# Revit family: RFL5
name_source: partatom
category: Lighting Fixtures
revit_build: Autodesk Revit 2014 (Build: 20130308_1515(x64)
units: mm (PartAtom-declared; Revit-internal decimal feet)

## types (1)
- RFL4
    Apparent Load = 265 VA
    Assembly Code = D5020200
    Certifications = UL 1598 Standard for Luminaires,IP66 certified.
    Color Filter = 16777215
    Connector Description = Lighting Connector
    Default Elevation = 48 "
    Description = Large LED flood with a variety of NEMA distribution for lighting applications such as safety/security, accent, flag pole, columns, or signs. The Ratio flood series was designed in cohesion with the site/area products to provide a sleek yet timeless product family to be used throughout a site. Ratio features a dense optical array which provides reduced pixelation and increased visual comfort without compromising performance.
    Dimming Lamp Color Temperature Shift = <None>
    Features = 3000K, 4000K, 5000K (70CRI)
18,000/25,000/32,000 Lumens
IP66
120-277V, 120V, 208V, 240V, 277V, 347V, 480V
130/190/265W
Knuckle and Trunnion mount
Narrow, Medium Flood, Wide Flood Distribution
NX Distributed Intelligence™ and 7-Pin with networked controls
Surge Protection
25.7LBS (11.66KG)
    Housing Material = Paint - Hubbell - Carbon Black
    LED = RFL
    LED_Finish = Glass - Hubbell - White
    Lamp = LED
    Length = 26.38 "
    Load Classification = Lighting
    Manufacturer = Hubbell Lighting
    Model = RFL5
    Photometric Note = For more ies file please find the above Photometric Web Link
    Photometric Web File = RFL5-360L-265-4K7-M.IES
    Photometric Web Link = https://www.hubbell.com
    Power Factor = 1
    Product Doucmentation Link = https://hubbellcdn.com
    Product Page URL = https://www.hubbell.com
    Reflector Finish = Hubbell - White Glass
    Screw = Metal-Hubbell-Gray
    Tilt Angle = 0.00°
    URL = https://www.hubbell.com
    Voltage = 120 V
    Warranty = 5 years Warranty
    Wattage Comments = 265W
    Watts = 265 W
    Width = 11.63 "
    Width 1 = 5 "

## geometry (parser evidence)
native form markers: Sweep x4
no freeform markers — native parametric forms only
